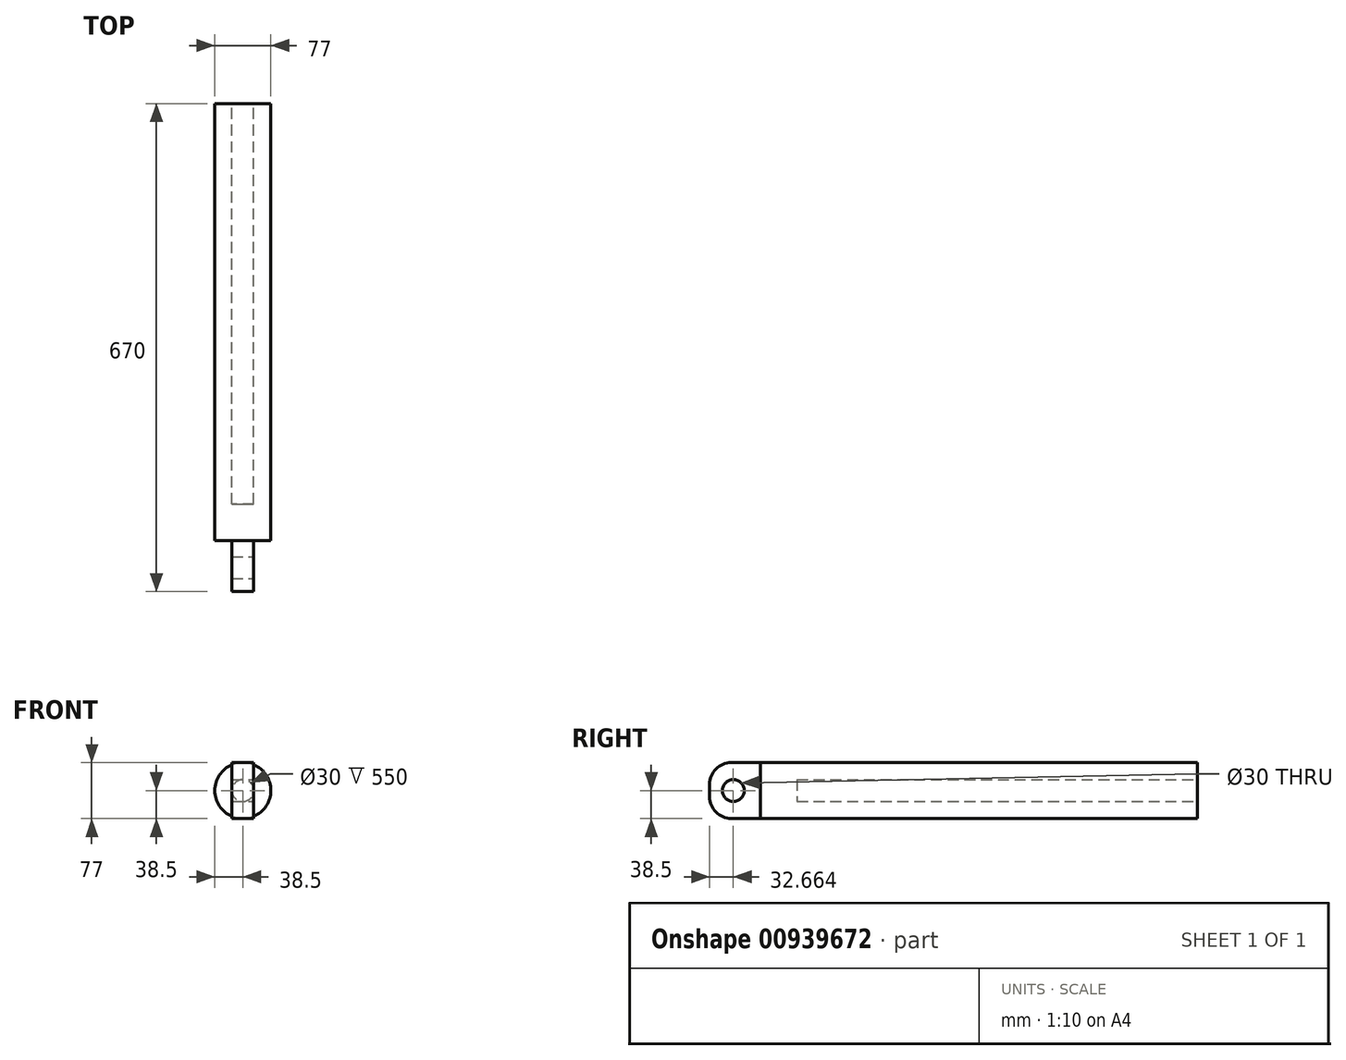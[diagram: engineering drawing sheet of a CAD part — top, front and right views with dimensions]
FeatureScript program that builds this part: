
annotation { "Feature Type Name" : "Feature", "Feature Type Description" : "" }
export const myFeature = defineFeature(function(context is Context, id is Id, definition is map)
    precondition{}
    {
        {
            var Q0;
            Q0=qCreatedBy(makeId("Front.planeOp"),FACE);
            var sketch = newSketch(context, id + "F0", { "sketchPlane" : qUnion([Q0])});
            skCircle(sketch, "E0", {"center": v(0, 0) * mm, "radius": 38.5 * mm});
            skSolve(sketch);
        }
        {
            var Q0;
            Q0 = qSketchRegion(id + "F0", true);
            extrude(context, id + "F1", {"entities" : qUnion([Q0]), "oppositeDirection" : true, "depth" : 600 * mm, "offsetDistance" : 25 * mm});
        }
        {
            var Q0;
            Q0=makeQuery(id+"F1.opExtrude","CAP_FACE",FACE,{"disambiguationData":[OSD([sQuery(id+"F0.wireOp",EDGE,"E0")])],"isStart":true});
            var sketch = newSketch(context, id + "F2", { "sketchPlane" : qUnion([Q0])});
            skLineSegment(sketch, "E1.bottom", {"start": v(15, -38.5) * mm, "end": v(-15, -38.5) * mm});
            skLineSegment(sketch, "E1.top", {"start": v(15, 38.5) * mm, "end": v(-15, 38.5) * mm});
            skLineSegment(sketch, "E1.left", {"start": v(15, -38.5) * mm, "end": v(15, 38.5) * mm});
            skLineSegment(sketch, "E1.right", {"start": v(-15, -38.5) * mm, "end": v(-15, 38.5) * mm});
            skPoint(sketch, "E1.middle", {"position": v(0, 0) * mm});
            skSolve(sketch);
        }
        {
            var Q0;
            Q0 = qSketchRegion(id + "F2", true);
            extrude(context, id + "F3", {"entities" : qUnion([Q0]), "operationType" : NewBodyOperationType.ADD, "depth" : 70 * mm, "offsetDistance" : 25 * mm});
        }
        {
            var Q0;
            Q0=makeQuery(id+"F3.opExtrude","SWEPT_FACE",FACE,{"disambiguationData":[OSD([sQuery(id+"F2.wireOp",EDGE,"E1.left")])]});
            var sketch = newSketch(context, id + "F4", { "sketchPlane" : qUnion([Q0])});
            skCircle(sketch, "E2", {"center": v(-37.34, 0) * mm, "radius": 15 * mm});
            skSolve(sketch);
        }
        {
            var Q0;
            Q0=makeQuery(id+"F4.imprint","IMPRINT",FACE,{"disambiguationData":[TD([[makeQuery(id+"F4.imprint","IMPRINT",EDGE,{"derivedFrom":sQuery(id+"F4.wireOp",EDGE,"E2")}),1.0]])]});
            extrude(context, id + "F5", {"entities" : qUnion([Q0]), "operationType" : NewBodyOperationType.REMOVE, "endBound" : BoundingType.THROUGH_ALL, "oppositeDirection" : true, "depth" : 25 * mm, "offsetDistance" : 25 * mm});
        }
        {
            var Q0;
            Q0=makeQuery(id+"F3.opExtrude","CAP_EDGE",EDGE,{"disambiguationData":[OSD([sQuery(id+"F2.wireOp",EDGE,"E1.top")])],"isStart":false});
            var Q1;
            Q1=makeQuery(id+"F3.opExtrude","CAP_EDGE",EDGE,{"disambiguationData":[OSD([sQuery(id+"F2.wireOp",EDGE,"E1.bottom")])],"isStart":false});
            fillet(context, id + "F6", {"entities" : qUnion([Q0, Q1]), "radius" : 30 * mm, "tangentPropagation" : true, "allowEdgeOverflow" : false});
        }
        {
            var Q0;
            Q0=makeQuery(id+"F1.opExtrude","CAP_FACE",FACE,{"disambiguationData":[OSD([sQuery(id+"F0.wireOp",EDGE,"E0")])],"isStart":false});
            var sketch = newSketch(context, id + "F7", { "sketchPlane" : qUnion([Q0])});
            skCircle(sketch, "E3", {"center": v(0, 0) * mm, "radius": 15 * mm});
            skSolve(sketch);
        }
        {
            var Q0;
            Q0=makeQuery(id+"F7.imprint","IMPRINT",FACE,{"disambiguationData":[TD([[makeQuery(id+"F7.imprint","IMPRINT",EDGE,{"derivedFrom":sQuery(id+"F7.wireOp",EDGE,"E3")}),1.0]])]});
            extrude(context, id + "F8", {"entities" : qUnion([Q0]), "operationType" : NewBodyOperationType.REMOVE, "oppositeDirection" : true, "depth" : 550 * mm, "offsetDistance" : 25 * mm});
        }
    });
